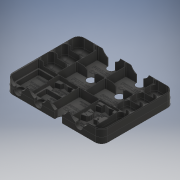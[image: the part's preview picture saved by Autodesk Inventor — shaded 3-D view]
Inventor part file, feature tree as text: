
AUTODESK INVENTOR PART (.ipt)
format: ipt  version: 2018 (Build 220112000, 112)  size: 7,114,752 bytes
history: native  units: mm
features: extrude x19, sketch x18, projected_geometry x7, revolve x2, fillet x1, sweep x1
ambient origin geometry x8: Origin, YZ Plane, XZ Plane, XY Plane, X Axis, Y Axis, Z Axis, Center Point
bodies: Solid1 (feature_tree)
feature tree (48):
  sketch  "Sketch1"  dims[d0=306.169469mm d1=232.509469mm]
  extrude  "Extrusion1"  Depth=232.509469mm
  extrude  "Extrusion2"  Depth=0.2mm
  extrude  "Extrusion3"  Depth=20.0mm
  fillet  "Fillet1"  Radius=90.5mm
  sketch  "Sketch3"  dims[d5=3.0mm d6=20.0mm d8=91.5mm d9=20.0mm d11=65.5mm d14=90.5mm]
  extrude  "Extrusion4"  Depth=1.0mm
  extrude  "Extrusion5"  Depth=1.0mm
  sweep  "Sweep1"
  extrude  "Extrusion6"  Depth=148.0mm
  extrude  "Extrusion7"  Depth=1.0mm
  extrude  "Extrusion8"  Depth=0.5mm
  extrude  "Extrusion9"  Depth=1.0mm
  extrude  "Extrusion12"  Depth=58.884735mm
  extrude  "Extrusion13"  Depth=40.5mm TaperAngle=0.0deg
  extrude  "Extrusion14"  Depth=260.0mm
  extrude  "Extrusion15"  Depth=2.0mm
  extrude  "Extrusion16"  Depth=12.0mm
  extrude  "Extrusion17"  Depth=2.1mm TaperAngle=0.0deg
  extrude  "Extrusion18"  Depth=31.0mm
  revolve  "Revolution1"  [1 undecoded]
  revolve  "Revolution2"  [1 undecoded]
  extrude  "Extrusion19"  Depth=31.0mm
  extrude  "Extrusion20"  TaperAngle=0.0deg  [1 undecoded]
  extrude  "Extrusion21"  Depth=31.0mm
  sketch  "Sketch2"  dims[d3=264.983911mm d4=0.2mm]
  projected_geometry  "Projected Loop1"
  sketch  "Sketch4"  dims[d15=64.5mm d16=1.0mm]
  sketch  "3D Sketch1"
  sketch  "Sketch5"  dims[d17=1.0mm d19=1.0mm]
  projected_geometry  "Projected Loop2"
  sketch  "Sketch7"  dims[d20=40.0mm d22=65.5mm d23=10.0mm d25=10.0mm d27=1.0mm]
  sketch  "Sketch8"  dims[d28=2.0mm d29=148.0mm]
  sketch  "Sketch9"  dims[d33=12.0mm d34=1.0mm]
  projected_geometry  "Projected Loop4"
  sketch  "Sketch10"  dims[d35=1.0mm d44=0.5mm]
  sketch  "Sketch11"  dims[d67=8.609469mm d68=1.0mm]
  sketch  "Sketch12"  dims[d69=1.0mm d70=58.884735mm]
  sketch  "Sketch13"  dims[d71=42.666667mm d76=40.5mm d77=0.0mm]
  sketch  "Sketch14"  dims[d78=1.0mm d79=0.0mm d80=260.0mm]
  projected_geometry  "Projected Loop6"
  sketch  "Sketch15"  dims[d81=220.0mm d82=2.0mm]
  projected_geometry  "Projected Loop7"
  sketch  "Sketch16"  dims[d83=12.0mm d84=0.0mm d85=12.0mm]
  projected_geometry  "Projected Loop8"
  sketch  "Sketch17"  dims[d86=80.0mm d87=213.0mm d88=52.0mm d90=1.0mm d91=56.0mm d95=2.1mm d96=0.0mm]
  projected_geometry  "Projected Loop9"
  sketch  "Sketch18"  dims[d97=3.1mm d98=0.0mm d99=18.33mm d100=0.349066mm d101=19.571469mm d102=11.303mm d103=0.0mm d104=0.0mm d105=20.4mm d106=0.0mm d107=15.9mm d108=0.0mm d109=14.4mm d110=0.0mm d111=78.645962mm d112=5.105088mm d113=30.0mm d114=0.75mm d115=39.641201mm d116=24.0mm d117=14.4mm d118=0.0mm d134=17.0mm d135=39.0mm d136=55.0mm d137=9.0mm d138=4.0mm d139=17.0mm d140=0.75mm d141=30.0mm d143=43.666667mm d144=10.0mm d146=10.0mm d148=14.0mm d149=0.0mm d150=20.0mm d152=131.0mm d153=10.0mm d155=10.0mm d157=72.0mm d158=41.0mm d159=53.0mm d160=16.0mm d161=4.5mm d162=0.0mm d163=4.1mm d164=0.0mm d165=0.75mm d166=22.0mm d167=16.0mm d168=10.0mm d169=41.0mm d170=0.75mm d171=2.0mm d172=0.0mm d173=1.0mm d176=4.0mm d178=56.5mm d179=74.5mm d180=4.0mm d181=4.0mm d182=12.0mm d183=2.0mm d184=0.0mm d185=4.0mm d186=56.5mm d187=35.0mm d188=4.0mm d189=1.515135mm d190=0.5mm d191=0.0mm d192=2.0mm d193=6.0mm d194=6.0mm d196=2.0mm d197=6.0mm d198=3.5mm d199=13.0mm d200=13.962634mm d201=8.726646mm d202=13.0mm d203=12.0mm d204=58.0mm d205=31.0mm d206=0.5mm d207=0.0mm d208=90.0deg d209=90.0deg d211=0.5mm d212=0.0mm d213=0.5mm d214=0.0mm d215=0.5mm d216=0.0mm]
note: 3 required parameter values undecoded (feature->parameter linkage not recoverable at this tier; creation-order binding heuristic only, values carry confidence <= 0.55)